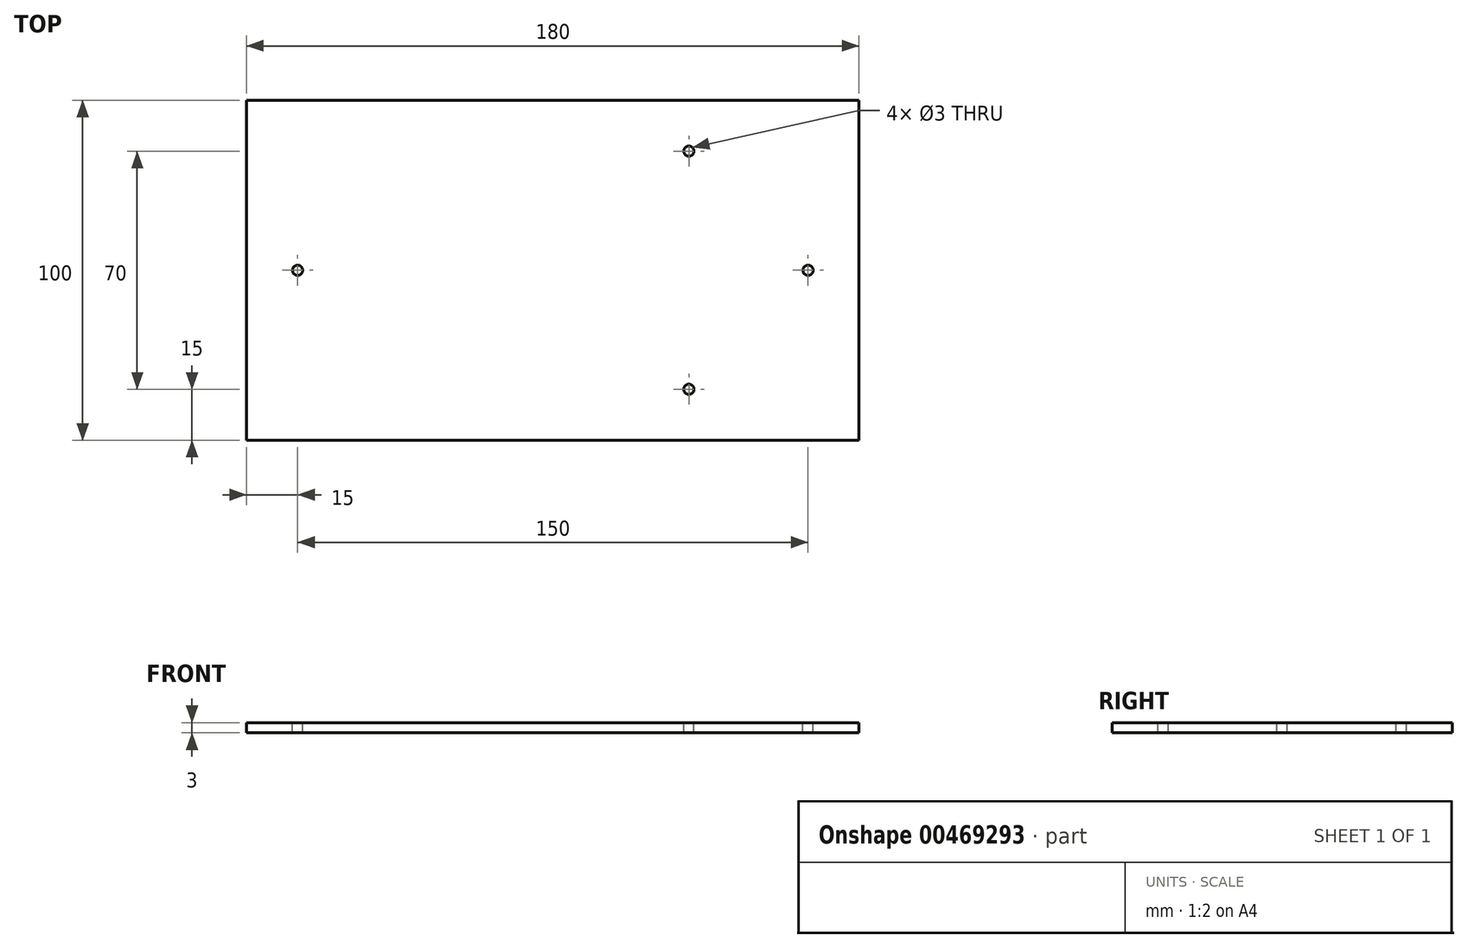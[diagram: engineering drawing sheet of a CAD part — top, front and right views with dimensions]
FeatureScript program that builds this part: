
annotation { "Feature Type Name" : "Feature", "Feature Type Description" : "" }
export const myFeature = defineFeature(function(context is Context, id is Id, definition is map)
    precondition{}
    {
        {
            var Q0;
            Q0=qCreatedBy(makeId("Top.planeOp"),FACE);
            var sketch = newSketch(context, id + "F0", { "sketchPlane" : qUnion([Q0])});
            skLineSegment(sketch, "E0.bottom", {"start": v(-90, 50) * mm, "end": v(90, 50) * mm});
            skLineSegment(sketch, "E0.top", {"start": v(-90, -50) * mm, "end": v(90, -50) * mm});
            skLineSegment(sketch, "E0.left", {"start": v(-90, 50) * mm, "end": v(-90, -50) * mm});
            skLineSegment(sketch, "E0.right", {"start": v(90, 50) * mm, "end": v(90, -50) * mm});
            skPoint(sketch, "E0.middle", {"position": v(0, 0) * mm});
            skSolve(sketch);
        }
        {
            var Q0;
            Q0 = qSketchRegion(id + "F0", true);
            extrude(context, id + "F1", {"entities" : qUnion([Q0]), "depth" : 3 * mm, "offsetDistance" : 25 * mm});
        }
        {
            var Q0;
            Q0=makeQuery(id+"F1.opExtrude","CAP_FACE",FACE,{"disambiguationData":[OSD([sQuery(id+"F0.wireOp",EDGE,"E0.bottom"),sQuery(id+"F0.wireOp",EDGE,"E0.top"),sQuery(id+"F0.wireOp",EDGE,"E0.left"),sQuery(id+"F0.wireOp",EDGE,"E0.right")])],"isStart":false});
            var sketch = newSketch(context, id + "F2", { "sketchPlane" : qUnion([Q0])});
            skPoint(sketch, "E1", {"position": v(75, 0) * mm});
            skPoint(sketch, "E2", {"position": v(-75, 0) * mm});
            skPoint(sketch, "E3", {"position": v(40, 35) * mm});
            skPoint(sketch, "E4", {"position": v(40, -35) * mm});
            skSolve(sketch);
        }
        {
            var Q0;
            Q0=sQuery(id+"F2.wireOp",VERTEX,"E2");
            var Q1;
            Q1=sQuery(id+"F2.wireOp",VERTEX,"E3");
            var Q2;
            Q2=sQuery(id+"F2.wireOp",VERTEX,"E1");
            var Q3;
            Q3=sQuery(id+"F2.wireOp",VERTEX,"E4");
            var Q4;
            Q4=makeQuery(id+"F1.opExtrude","SWEPT_BODY",BODY,{"disambiguationData":[OSD([sQuery(id+"F0.wireOp",EDGE,"E0.bottom"),sQuery(id+"F0.wireOp",EDGE,"E0.top"),sQuery(id+"F0.wireOp",EDGE,"E0.left"),sQuery(id+"F0.wireOp",EDGE,"E0.right")])]});
            hole(context, id + "F3", {"style" : HoleStyle.SIMPLE, "endStyle" : HoleEndStyle.THROUGH, "holeDiameter" : 3 * mm, "isTappedThrough" : true, "tappedDepth" : 12 * mm, "tapClearance" : 3, "locations" : qUnion([Q0, Q1, Q2, Q3]), "scope" : qUnion([Q4])});
        }
    });
